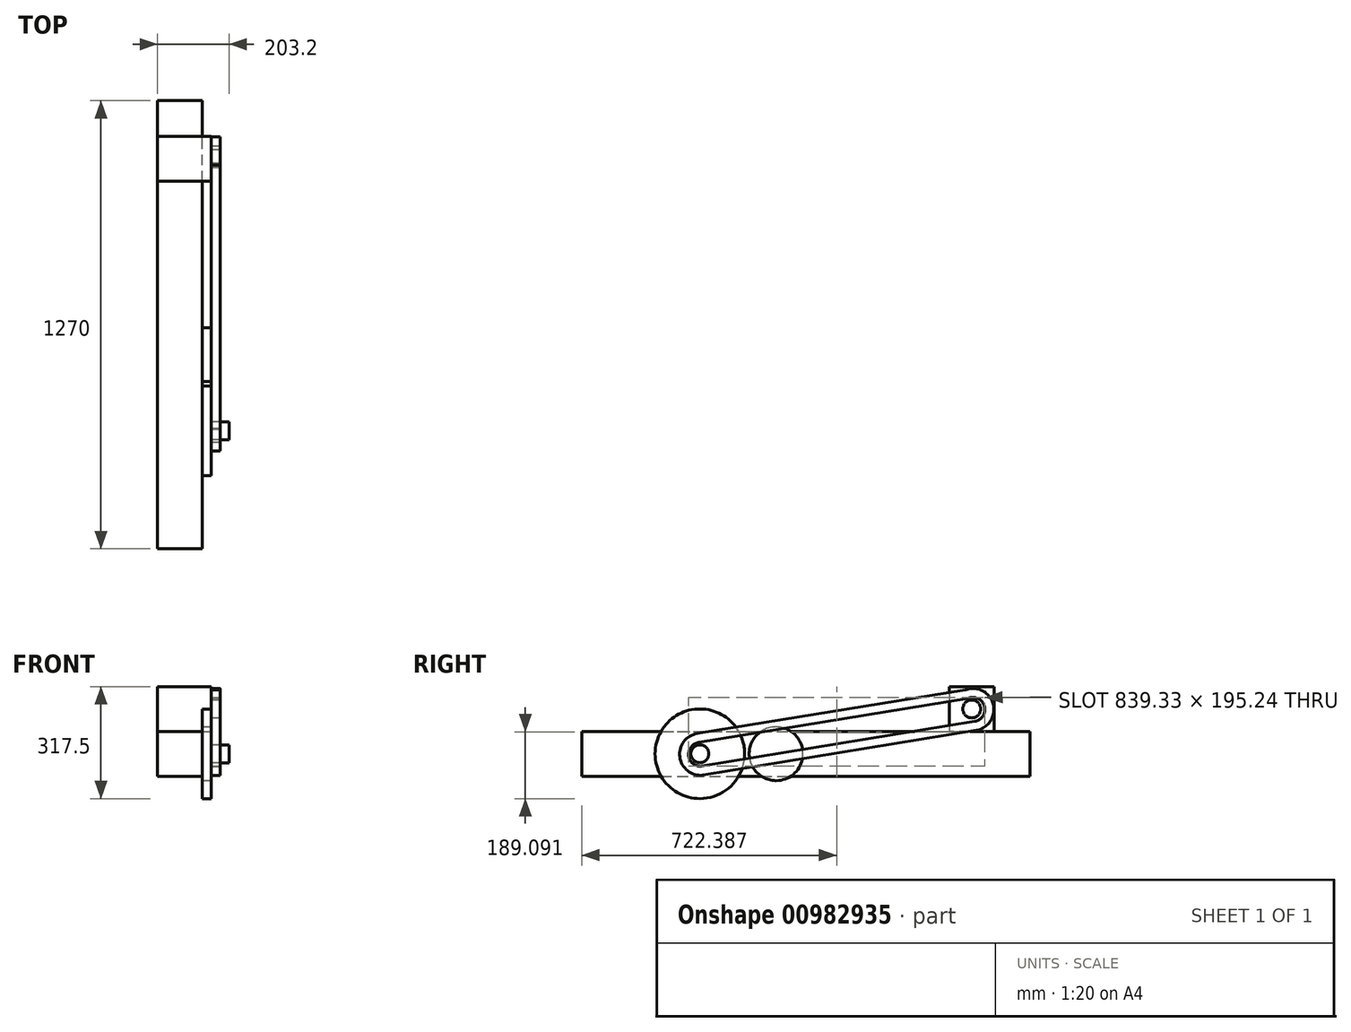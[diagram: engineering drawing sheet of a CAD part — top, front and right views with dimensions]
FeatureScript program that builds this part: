
annotation { "Feature Type Name" : "Feature", "Feature Type Description" : "" }
export const myFeature = defineFeature(function(context is Context, id is Id, definition is map)
    precondition{}
    {
        {
            var Q0;
            Q0=qCreatedBy(makeId("Right.planeOp"),FACE);
            var sketch = newSketch(context, id + "F0", { "sketchPlane" : qUnion([Q0])});
            skLineSegment(sketch, "E0.bottom", {"start": v(0, 0) * mm, "end": v(1270, 0) * mm});
            skLineSegment(sketch, "E0.top", {"start": v(0, -127) * mm, "end": v(1270, -127) * mm});
            skLineSegment(sketch, "E0.left", {"start": v(0, 0) * mm, "end": v(0, -127) * mm});
            skLineSegment(sketch, "E0.right", {"start": v(1270, 0) * mm, "end": v(1270, -127) * mm});
            skSolve(sketch);
        }
        {
            var Q0;
            Q0=qSketchRegion(id+"F0",true);
            extrude(context, id + "F1", {"entities" : qUnion([Q0]), "oppositeDirection" : true, "depth" : 127 * mm, "offsetDistance" : 25.4 * mm});
        }
        {
            var Q0;
            Q0=makeQuery(id+"F1.opExtrude","CAP_FACE",FACE,{"disambiguationData":[OSD([sQuery(id+"F0.wireOp",EDGE,"E0.bottom"),sQuery(id+"F0.wireOp",EDGE,"E0.top"),sQuery(id+"F0.wireOp",EDGE,"E0.left"),sQuery(id+"F0.wireOp",EDGE,"E0.right")])],"isStart":true});
            var sketch = newSketch(context, id + "F2", { "sketchPlane" : qUnion([Q0])});
            skCircle(sketch, "E1", {"center": v(334.44, -63.5) * mm, "radius": 127 * mm});
            skPoint(sketch, "E1.centerSnap0", {"position": v(0, -63.5) * mm});
            skCircle(sketch, "E2", {"center": v(550.34, -63.5) * mm, "radius": 76.2 * mm});
            skSolve(sketch);
        }
        {
            var Q0;
            Q0=qSketchRegion(id+"F2",true);
            extrude(context, id + "F3", {"entities" : qUnion([Q0]), "operationType" : NewBodyOperationType.ADD, "depth" : 25.4 * mm, "offsetDistance" : 25.4 * mm});
        }
        {
            var Q0;
            Q0=makeQuery(id+"F3.opExtrude","CAP_FACE",FACE,{"disambiguationData":[OSD([sQuery(id+"F2.wireOp",EDGE,"E1")])],"isStart":false});
            var sketch = newSketch(context, id + "F4", { "sketchPlane" : qUnion([Q0])});
            skCircle(sketch, "E3", {"center": v(334.44, -63.5) * mm, "radius": 25.4 * mm});
            skSolve(sketch);
        }
        {
            var Q0;
            Q0=qSketchRegion(id+"F4",true);
            extrude(context, id + "F5", {"entities" : qUnion([Q0]), "operationType" : NewBodyOperationType.ADD, "depth" : 50.8 * mm, "offsetDistance" : 25.4 * mm});
        }
        {
            var Q0;
            Q0=makeQuery(id+"F1.opExtrude","SWEPT_FACE",FACE,{"disambiguationData":[OSD([sQuery(id+"F0.wireOp",EDGE,"E0.bottom")])]});
            var sketch = newSketch(context, id + "F6", { "sketchPlane" : qUnion([Q0])});
            skLineSegment(sketch, "E4.bottom", {"start": v(-127, 1168.4) * mm, "end": v(25.4, 1168.4) * mm});
            skLineSegment(sketch, "E4.top", {"start": v(-127, 1041.4) * mm, "end": v(25.4, 1041.4) * mm});
            skLineSegment(sketch, "E4.left", {"start": v(-127, 1168.4) * mm, "end": v(-127, 1041.4) * mm});
            skLineSegment(sketch, "E4.right", {"start": v(25.4, 1168.4) * mm, "end": v(25.4, 1041.4) * mm});
            skSolve(sketch);
        }
        {
            var Q0;
            Q0=qSketchRegion(id+"F6",true);
            extrude(context, id + "F7", {"entities" : qUnion([Q0]), "operationType" : NewBodyOperationType.ADD, "depth" : 127 * mm, "offsetDistance" : 25.4 * mm});
        }
        {
            var Q0;
            Q0=makeQuery(id+"F7.opExtrude","SWEPT_FACE",FACE,{"disambiguationData":[OSD([sQuery(id+"F6.wireOp",EDGE,"E4.right")])]});
            var sketch = newSketch(context, id + "F8", { "sketchPlane" : qUnion([Q0])});
            skCircle(sketch, "E5", {"center": v(1104.9, 63.5) * mm, "radius": 25.4 * mm});
            skPoint(sketch, "E5.centerSnap0", {"position": v(1041.4, 63.5) * mm});
            skPoint(sketch, "E5.centerSnap1", {"position": v(1104.9, 0) * mm});
            skSolve(sketch);
        }
        {
            var Q0;
            Q0=makeQuery(id+"F8.imprint","IMPRINT",FACE,{"disambiguationData":[TD([[makeQuery(id+"F8.imprint","IMPRINT",EDGE,{"derivedFrom":sQuery(id+"F8.wireOp",EDGE,"E5")}),1.0]])]});
            extrude(context, id + "F9", {"entities" : qUnion([Q0]), "operationType" : NewBodyOperationType.ADD, "depth" : 25.4 * mm, "offsetDistance" : 25.4 * mm});
        }
        {
            var Q0;
            Q0=makeQuery(id+"F9.opExtrude","CAP_FACE",FACE,{"disambiguationData":[OSD([sQuery(id+"F8.wireOp",EDGE,"E5")])],"isStart":false});
            var sketch = newSketch(context, id + "F10", { "sketchPlane" : qUnion([Q0])});
            skLineSegment(sketch, "E6", {"start": v(1094.43, 93.4) * mm, "end": v(331.11, -31.3) * mm});
            skLineSegment(sketch, "E7", {"start": v(1113.6, 28) * mm, "end": v(339.3, -99.03) * mm});
            skArc(sketch, "E8", {"start": v(331.11, -31.3) * mm, "mid": v(302.72, -69.1) * mm, "end": v(339.3, -99.03) * mm});
            skArc(sketch, "E9", {"start": v(1113.6, 28) * mm, "mid": v(1141, 71.53) * mm, "end": v(1094.43, 93.4) * mm});
            skArc(sketch, "E10.0", {"start": v(1117.7, 2.93) * mm, "mid": v(1165.84, 76.96) * mm, "end": v(1087.68, 118.04) * mm});
            skLineSegment(sketch, "E10.1", {"start": v(1117.7, 2.93) * mm, "end": v(342.5, -124.25) * mm});
            skArc(sketch, "E10.2", {"start": v(327.01, -6.24) * mm, "mid": v(277.58, -72.74) * mm, "end": v(342.5, -124.25) * mm});
            skLineSegment(sketch, "E10.3", {"start": v(1087.68, 118.04) * mm, "end": v(327.01, -6.24) * mm});
            skSolve(sketch);
        }
        {
            var Q0;
            Q0=makeQuery(id+"F10.imprint","IMPRINT",FACE,{"disambiguationData":[TD([[makeQuery(id+"F10.imprint","IMPRINT",EDGE,{"derivedFrom":sQuery(id+"F10.wireOp",EDGE,"E6")}),-1.0]])]});
            extrude(context, id + "F11", {"entities" : qUnion([Q0]), "oppositeDirection" : true, "depth" : 25.4 * mm, "offsetDistance" : 25.4 * mm});
        }
    });
